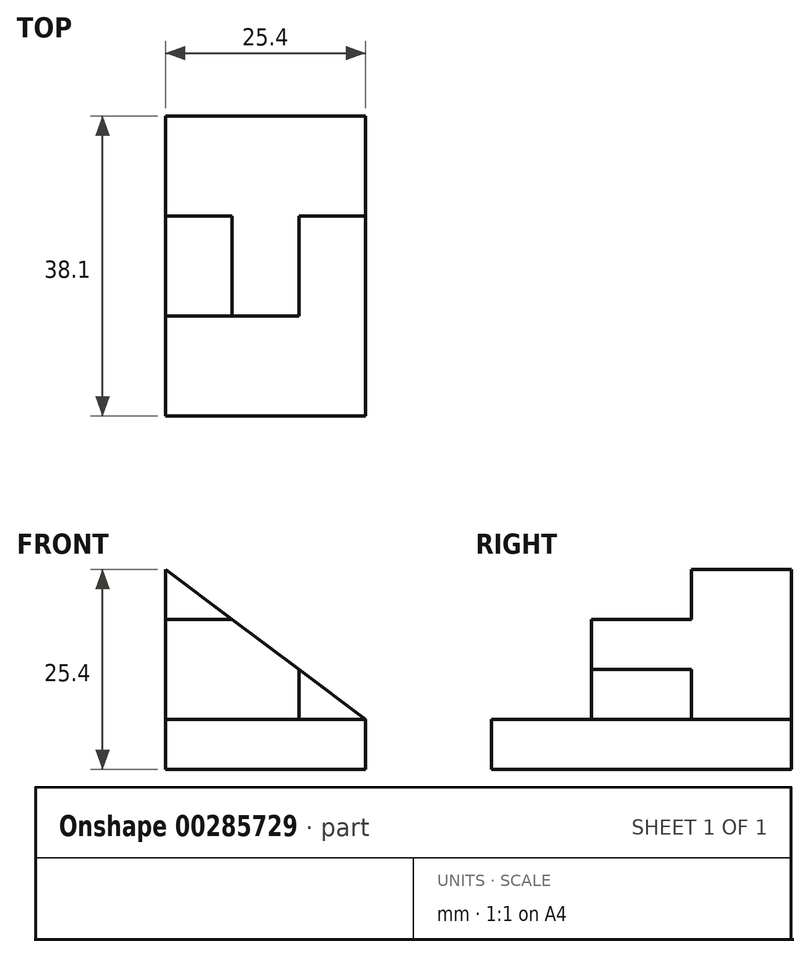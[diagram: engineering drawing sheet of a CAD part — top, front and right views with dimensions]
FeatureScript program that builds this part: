
annotation { "Feature Type Name" : "Feature", "Feature Type Description" : "" }
export const myFeature = defineFeature(function(context is Context, id is Id, definition is map)
    precondition{}
    {
        {
            var Q0;
            Q0=qCreatedBy(makeId("Front.planeOp"),FACE);
            var sketch = newSketch(context, id + "F0", { "sketchPlane" : qUnion([Q0])});
            skLineSegment(sketch, "E0", {"start": v(0, 0) * mm, "end": v(0, 6.35) * mm});
            skLineSegment(sketch, "E1", {"start": v(0, 6.35) * mm, "end": v(25.4, 6.35) * mm});
            skLineSegment(sketch, "E2", {"start": v(25.4, 0) * mm, "end": v(0, 0) * mm});
            skLineSegment(sketch, "E3", {"start": v(25.4, 0) * mm, "end": v(25.4, 6.35) * mm});
            skLineSegment(sketch, "E4", {"start": v(25.4, 6.35) * mm, "end": v(0, 25.4) * mm});
            skLineSegment(sketch, "E5", {"start": v(0, 25.4) * mm, "end": v(0, 6.35) * mm});
            skLineSegment(sketch, "E6", {"start": v(16.93, 12.7) * mm, "end": v(16.93, 6.35) * mm});
            skLineSegment(sketch, "E7", {"start": v(0, 19.05) * mm, "end": v(8.47, 19.05) * mm});
            skSolve(sketch);
        }
        {
            var Q0;
            {var subQ3=sQuery(id+"F0.wireOp",EDGE,"E7");Q0=makeQuery(id+"F0.imprint","IMPRINT",FACE,{"disambiguationData":[TD([[makeQuery(id+"F0.imprint","IMPRINT",EDGE,{"derivedFrom":subQ3}),1.0]])]});}
            var Q1;
            {var subQ0=sQuery(id+"F0.wireOp",EDGE,"E6");Q1=makeQuery(id+"F0.imprint","IMPRINT",FACE,{"disambiguationData":[TD([[makeQuery(id+"F0.imprint","IMPRINT",EDGE,{"derivedFrom":subQ0}),-1.0]])]});}
            var Q2;
            {var subQ3=sQuery(id+"F0.wireOp",EDGE,"E0");Q2=makeQuery(id+"F0.imprint","IMPRINT",FACE,{"disambiguationData":[TD([[makeQuery(id+"F0.imprint","IMPRINT",EDGE,{"derivedFrom":subQ3}),-1.0]])]});}
            var Q3;
            {var subQ3=sQuery(id+"F0.wireOp",EDGE,"E6");Q3=makeQuery(id+"F0.imprint","IMPRINT",FACE,{"disambiguationData":[TD([[makeQuery(id+"F0.imprint","IMPRINT",EDGE,{"derivedFrom":subQ3}),1.0]])]});}
            extrude(context, id + "F1", {"entities" : qUnion([Q0, Q1, Q2, Q3]), "oppositeDirection" : true, "depth" : 38.1 * mm});
        }
        {
            var Q0;
            {var subQ3=sQuery(id+"F0.wireOp",EDGE,"E7");Q0=makeQuery(id+"F0.imprint","IMPRINT",FACE,{"disambiguationData":[TD([[makeQuery(id+"F0.imprint","IMPRINT",EDGE,{"derivedFrom":subQ3}),1.0]])]});}
            extrude(context, id + "F2", {"entities" : qUnion([Q0]), "operationType" : NewBodyOperationType.REMOVE, "oppositeDirection" : true, "depth" : 25.4 * mm});
        }
        {
            var Q0;
            {var subQ3=sQuery(id+"F0.wireOp",EDGE,"E6");Q0=makeQuery(id+"F0.imprint","IMPRINT",FACE,{"disambiguationData":[TD([[makeQuery(id+"F0.imprint","IMPRINT",EDGE,{"derivedFrom":subQ3}),1.0]])]});}
            extrude(context, id + "F3", {"entities" : qUnion([Q0]), "operationType" : NewBodyOperationType.REMOVE, "oppositeDirection" : true, "depth" : 25.4 * mm});
        }
        {
            var Q0;
            {var subQ0=sQuery(id+"F0.wireOp",EDGE,"E6");Q0=makeQuery(id+"F0.imprint","IMPRINT",FACE,{"disambiguationData":[TD([[makeQuery(id+"F0.imprint","IMPRINT",EDGE,{"derivedFrom":subQ0}),-1.0]])]});}
            extrude(context, id + "F4", {"entities" : qUnion([Q0]), "operationType" : NewBodyOperationType.REMOVE, "oppositeDirection" : true, "depth" : 12.7 * mm});
        }
    });
